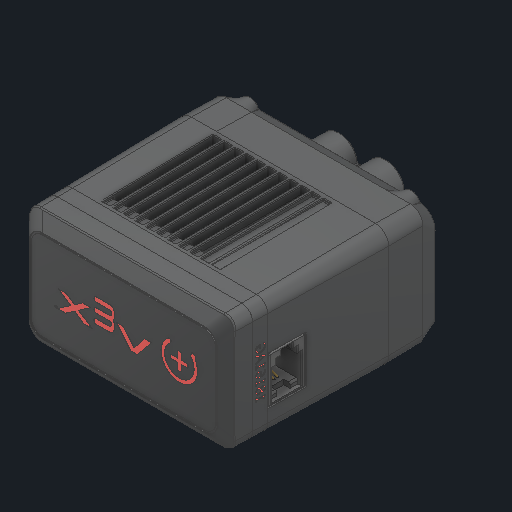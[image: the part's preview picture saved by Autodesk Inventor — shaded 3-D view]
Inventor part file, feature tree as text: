
AUTODESK INVENTOR PART (.ipt)
format: ipt  version: 2025 (Build 290162000, 162)  size: 13,097,472 bytes
history: native  units: in
note: dims shown in document units (in); Inventor stores cm internally (conversion verified against a paired STEP export)
features: other x19, sketch x2
ambient origin geometry x8: Origin, YZ Plane, XZ Plane, XY Plane, X Axis, Y Axis, Z Axis, Center Point
bodies: Solid1 (feature_tree), Solid2 (feature_tree), Solid7 (feature_tree), Solid8 (feature_tree), Solid9 (feature_tree), Solid20 (feature_tree), Solid21 (feature_tree), Solid22 (feature_tree)
feature tree (21):
  other  "V5 Motor.ipt"
  other  "Solid1::V5 Motor.ipt"
  other  "Solid2::V5 Motor.ipt"
  other  "Solid4::V5 Motor.ipt"
  other  "Solid6::V5 Motor.ipt"
  other  "Solid7::V5 Motor.ipt"
  other  "Solid8::V5 Motor.ipt"
  other  "Solid9::V5 Motor.ipt"
  other  "Solid14::V5 Motor.ipt"
  other  "Solid16::V5 Motor.ipt"
  other  "Solid17::V5 Motor.ipt"
  other  "Solid18::V5 Motor.ipt"
  other  "Solid19::V5 Motor.ipt"
  other  "Solid20::V5 Motor.ipt"
  other  "Solid21::V5 Motor.ipt"
  other  "Solid22::V5 Motor.ipt"
  other  "TaggingFeature1"
  sketch  "Sketch1"  dims[d0=0.3937in]
  sketch  "Sketch2"  dims[d4=0.0in d5=0.0in]
  other  "iInsert:1"
  other  "iInsert:2"
